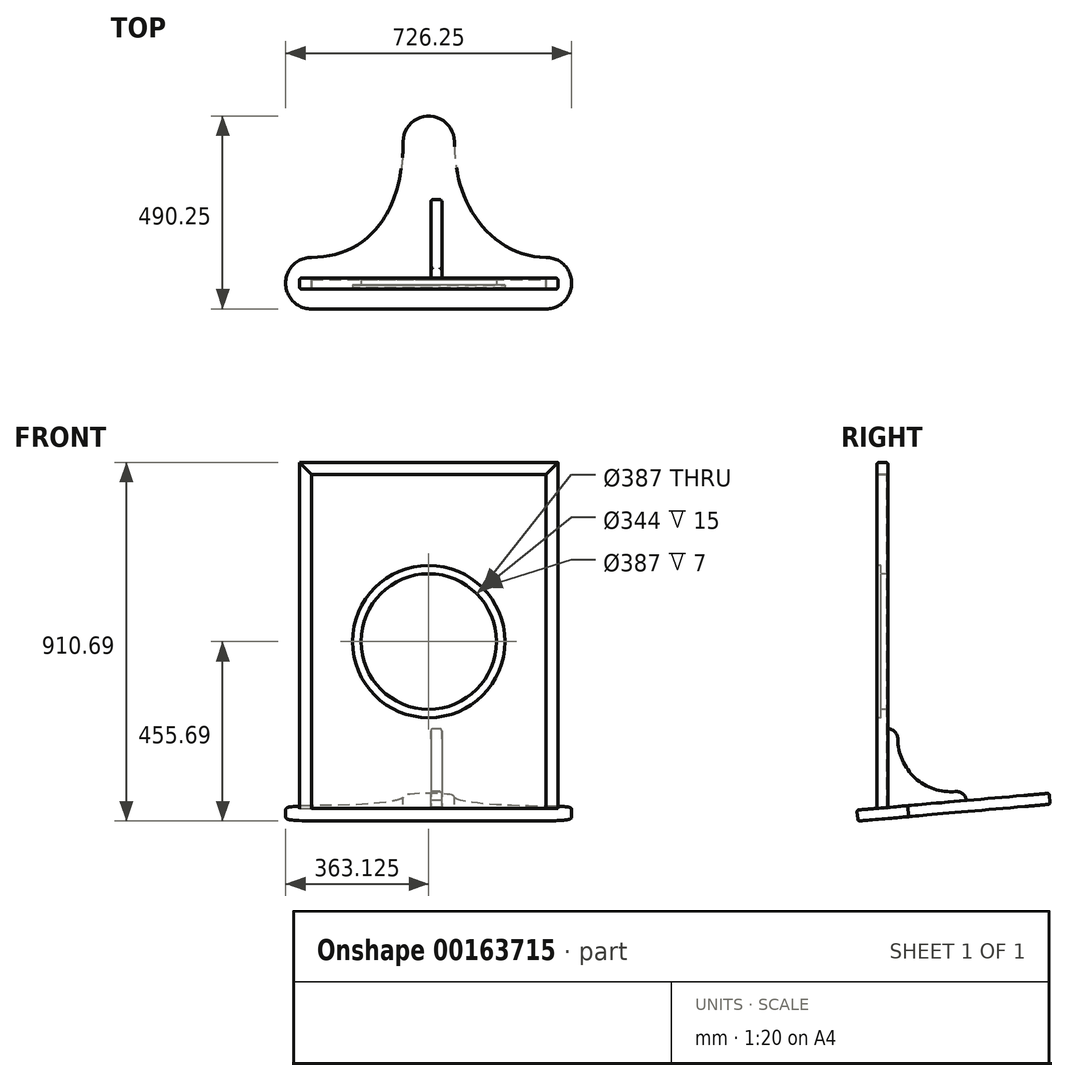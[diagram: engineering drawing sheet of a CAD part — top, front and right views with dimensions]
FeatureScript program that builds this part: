
annotation { "Feature Type Name" : "Feature", "Feature Type Description" : "" }
export const myFeature = defineFeature(function(context is Context, id is Id, definition is map)
    precondition{}
    {
        {
            var Q0;
            Q0=qCreatedBy(makeId("Front.planeOp"),FACE);
            var sketch = newSketch(context, id + "F0", { "sketchPlane" : qUnion([Q0])});
            skLineSegment(sketch, "E0.bottom", {"start": v(0, 0) * mm, "end": v(596.25, 0) * mm});
            skLineSegment(sketch, "E0.top", {"start": v(0, 850) * mm, "end": v(596.25, 850) * mm});
            skLineSegment(sketch, "E0.left", {"start": v(0, 0) * mm, "end": v(0, 850) * mm});
            skLineSegment(sketch, "E0.right", {"start": v(596.25, 0) * mm, "end": v(596.25, 850) * mm});
            skSolve(sketch);
        }
        {
            var Q0;
            Q0 = qSketchRegion(id + "F0", true);
            extrude(context, id + "F1", {"entities" : qUnion([Q0]), "depth" : (2 * 11) * mm, "symmetric" : true});
        }
        {
            var Q0;
            Q0=makeQuery(id+"F1.opExtrude","CAP_FACE",FACE,{"disambiguationData":[OSD([sQuery(id+"F0.wireOp",EDGE,"E0.bottom"),sQuery(id+"F0.wireOp",EDGE,"E0.top"),sQuery(id+"F0.wireOp",EDGE,"E0.left"),sQuery(id+"F0.wireOp",EDGE,"E0.right")])],"isStart":false});
            var sketch = newSketch(context, id + "F2", { "sketchPlane" : qUnion([Q0])});
            skLineSegment(sketch, "E1.0.0", {"start": v(596.25, 850) * mm, "end": v(0, 850) * mm});
            skLineSegment(sketch, "E1.0.1", {"start": v(0, 850) * mm, "end": v(0, 0) * mm});
            skLineSegment(sketch, "E1.0.2", {"start": v(0, 0) * mm, "end": v(596.25, 0) * mm});
            skLineSegment(sketch, "E1.0.3", {"start": v(596.25, 0) * mm, "end": v(596.25, 850) * mm});
            skSolve(sketch);
        }
        {
            var Q0;
            Q0 = qSketchRegion(id + "F2", true);
            extrude(context, id + "F3", {"entities" : qUnion([Q0]), "depth" : 3 * mm});
        }
        {
            var Q0;
            Q0=makeQuery(id+"F3.opExtrude","SWEPT_BODY",BODY,{"disambiguationData":[OSD([sQuery(id+"F2.wireOp",EDGE,"E1.0.0"),sQuery(id+"F2.wireOp",EDGE,"E1.0.1"),sQuery(id+"F2.wireOp",EDGE,"E1.0.2"),sQuery(id+"F2.wireOp",EDGE,"E1.0.3")])]});
            var Q1;
            Q1=qCreatedBy(makeId("Front.planeOp"),FACE);
            mirror(context, id + "F4", {"entities" : qUnion([Q0]), "mirrorPlane" : qUnion([Q1])});
        }
        {
            var Q0;
            Q0=qCreatedBy(makeId("Front.planeOp"),FACE);
            var sketch = newSketch(context, id + "F5", { "sketchPlane" : qUnion([Q0])});
            skLineSegment(sketch, "E2", {"start": v(-30, 0) * mm, "end": v(-30, 880) * mm});
            skLineSegment(sketch, "E3", {"start": v(-30, 880) * mm, "end": v(0, 850) * mm});
            skLineSegment(sketch, "E4", {"start": v(0, 850) * mm, "end": v(0, 0) * mm});
            skLineSegment(sketch, "E5", {"start": v(0, 0) * mm, "end": v(-30, 0) * mm});
            skLineSegment(sketch, "E6", {"start": v(596.25, 0) * mm, "end": v(596.25, 850) * mm});
            skLineSegment(sketch, "E7", {"start": v(596.25, 850) * mm, "end": v(626.25, 880) * mm});
            skLineSegment(sketch, "E8", {"start": v(626.25, 880) * mm, "end": v(626.25, 0) * mm});
            skLineSegment(sketch, "E9", {"start": v(626.25, 0) * mm, "end": v(596.25, 0) * mm});
            skSolve(sketch);
        }
        {
            var Q0;
            Q0 = qSketchRegion(id + "F5", true);
            var Q1;
            Q1=makeQuery(id+"F4.opPattern","COPY",FACE,{"derivedFrom":makeQuery(id+"F3.opExtrude","CAP_FACE",FACE,{"disambiguationData":[OSD([sQuery(id+"F2.wireOp",EDGE,"E1.0.0"),sQuery(id+"F2.wireOp",EDGE,"E1.0.1"),sQuery(id+"F2.wireOp",EDGE,"E1.0.2"),sQuery(id+"F2.wireOp",EDGE,"E1.0.3")])],"isStart":false}),"instanceName":"1"});
            extrude(context, id + "F6", {"entities" : qUnion([Q0]), "oppositeDirection" : true, "endBoundEntityFace" : qUnion([Q1]), "depth" : (2 * 11 + 2 * 3) * mm, "symmetric" : true});
        }
        {
            var Q0;
            Q0=makeQuery(id+"F3.opExtrude","CAP_FACE",FACE,{"disambiguationData":[OSD([sQuery(id+"F2.wireOp",EDGE,"E1.0.0"),sQuery(id+"F2.wireOp",EDGE,"E1.0.1"),sQuery(id+"F2.wireOp",EDGE,"E1.0.2"),sQuery(id+"F2.wireOp",EDGE,"E1.0.3")])],"isStart":false});
            var sketch = newSketch(context, id + "F7", { "sketchPlane" : qUnion([Q0])});
            skLineSegment(sketch, "E10", {"start": v(-30, 880) * mm, "end": v(0, 850) * mm});
            skLineSegment(sketch, "E11", {"start": v(0, 850) * mm, "end": v(596.25, 850) * mm});
            skLineSegment(sketch, "E12", {"start": v(596.25, 850) * mm, "end": v(626.25, 880) * mm});
            skLineSegment(sketch, "E13", {"start": v(626.25, 880) * mm, "end": v(-30, 880) * mm});
            skSolve(sketch);
        }
        {
            var Q0;
            Q0 = qSketchRegion(id + "F7", true);
            var Q1;
            Q1=makeQuery(id+"F4.opPattern","COPY",FACE,{"derivedFrom":makeQuery(id+"F3.opExtrude","CAP_FACE",FACE,{"disambiguationData":[OSD([sQuery(id+"F2.wireOp",EDGE,"E1.0.0"),sQuery(id+"F2.wireOp",EDGE,"E1.0.1"),sQuery(id+"F2.wireOp",EDGE,"E1.0.2"),sQuery(id+"F2.wireOp",EDGE,"E1.0.3")])],"isStart":false}),"instanceName":"1"});
            extrude(context, id + "F8", {"entities" : qUnion([Q0]), "endBound" : BoundingType.UP_TO_SURFACE, "oppositeDirection" : true, "endBoundEntityFace" : qUnion([Q1]), "depth" : 25 * mm});
        }
        {
            var Q0;
            Q0=makeQuery(id+"F3.opExtrude","CAP_FACE",FACE,{"disambiguationData":[OSD([sQuery(id+"F2.wireOp",EDGE,"E1.0.0"),sQuery(id+"F2.wireOp",EDGE,"E1.0.1"),sQuery(id+"F2.wireOp",EDGE,"E1.0.2"),sQuery(id+"F2.wireOp",EDGE,"E1.0.3")])],"isStart":false});
            var sketch = newSketch(context, id + "F9", { "sketchPlane" : qUnion([Q0])});
            skCircle(sketch, "E14", {"center": v(298.12, 425) * mm, "radius": 172 * mm});
            skPoint(sketch, "E14.centerSnap0", {"position": v(596.25, 425) * mm});
            skPoint(sketch, "E14.centerSnap1", {"position": v(298.12, 850) * mm});
            skSolve(sketch);
        }
        {
            var Q0;
            Q0 = qSketchRegion(id + "F9", true);
            extrude(context, id + "F10", {"entities" : qUnion([Q0]), "operationType" : NewBodyOperationType.REMOVE, "endBound" : BoundingType.THROUGH_ALL, "oppositeDirection" : true, "depth" : 25 * mm});
        }
        {
            var Q0;
            Q0=makeQuery(id+"F3.opExtrude","CAP_FACE",FACE,{"disambiguationData":[OSD([sQuery(id+"F2.wireOp",EDGE,"E1.0.0"),sQuery(id+"F2.wireOp",EDGE,"E1.0.1"),sQuery(id+"F2.wireOp",EDGE,"E1.0.2"),sQuery(id+"F2.wireOp",EDGE,"E1.0.3")])],"isStart":false});
            var sketch = newSketch(context, id + "F11", { "sketchPlane" : qUnion([Q0])});
            skCircle(sketch, "E15", {"center": v(298.12, 425) * mm, "radius": 193.5 * mm});
            skSolve(sketch);
        }
        {
            var Q0;
            Q0 = qSketchRegion(id + "F11", true);
            extrude(context, id + "F12", {"entities" : qUnion([Q0]), "operationType" : NewBodyOperationType.REMOVE, "oppositeDirection" : true, "depth" : 10 * mm});
        }
        {
            var Q0;
            Q0=makeQuery(id+"F1.opExtrude","SWEPT_FACE",FACE,{"disambiguationData":[OSD([sQuery(id+"F0.wireOp",EDGE,"E0.left")])]});
            var sketch = newSketch(context, id + "F13", { "sketchPlane" : qUnion([Q0])});
            skLineSegment(sketch, "E16", {"start": v(52.79, -2.17) * mm, "end": v(-51.83, 6.98) * mm});
            skLineSegment(sketch, "E17", {"start": v(-51.83, 6.98) * mm, "end": v(-51.83, -8.68) * mm});
            skLineSegment(sketch, "E18", {"start": v(-51.83, -8.68) * mm, "end": v(52.79, -20.76) * mm});
            skLineSegment(sketch, "E19", {"start": v(52.79, -20.76) * mm, "end": v(52.79, -2.17) * mm});
            skLineSegment(sketch, "E20", {"start": v(0, 0) * mm, "end": v(-74.05, 0) * mm, "construction": true});
            skSolve(sketch);
        }
        {
            var Q0;
            Q0 = qSketchRegion(id + "F13", true);
            extrude(context, id + "F14", {"entities" : qUnion([Q0]), "operationType" : NewBodyOperationType.REMOVE, "endBound" : BoundingType.THROUGH_ALL, "oppositeDirection" : true, "depth" : 25 * mm});
        }
        {
            var Q0;
            Q0=makeQuery(id+"F14.boolean.opBoolean","COPY",FACE,{"derivedFrom":makeQuery(id+"F14.opExtrude","SWEPT_FACE",FACE,{"disambiguationData":[OSD([sQuery(id+"F13.wireOp",EDGE,"E16")])]})});
            var sketch = newSketch(context, id + "F15", { "sketchPlane" : qUnion([Q0])});
            skLineSegment(sketch, "E21", {"start": v(0, 64.79) * mm, "end": v(596.25, 64.79) * mm});
            skLineSegment(sketch, "E22", {"start": v(596.25, -247.71) * mm, "end": v(596.25, 344.4) * mm, "construction": true});
            skLineSegment(sketch, "E23", {"start": v(298.13, 283.82) * mm, "end": v(298.13, -740.69) * mm, "construction": true});
            skLineSegment(sketch, "E24", {"start": v(0, 0) * mm, "end": v(0, -312.02) * mm, "construction": true});
            skLineSegment(sketch, "E25.0", {"start": v(0, -11.26) * mm, "end": v(0, -11.26) * mm});
            skLineSegment(sketch, "E26", {"start": v(0, 0) * mm, "end": v(0, 138.52) * mm, "construction": true});
            skArc(sketch, "E27", {"start": v(0, 64.79) * mm, "mid": v(-65, -0.21) * mm, "end": v(0, -65.21) * mm});
            skArc(sketch, "E28", {"start": v(596.25, 64.79) * mm, "mid": v(661.25, -0.21) * mm, "end": v(596.25, -65.21) * mm});
            skArc(sketch, "E29", {"start": v(233.13, -360.72) * mm, "mid": v(298.13, -425.72) * mm, "end": v(363.13, -360.72) * mm});
            skFitSpline(sketch, "E30", {"points": [v(0, -65.21) * mm, v(233.13, -360.72) * mm], "startDerivative": vector(399.52, 0) * mm, "endDerivative": vector(0, -583.63) * mm});
            skFitSpline(sketch, "E31", {"points": [v(363.13, -360.72) * mm, v(596.25, -65.21) * mm], "startDerivative": vector(0, 583.63) * mm, "endDerivative": vector(331.66, 0) * mm});
            skSolve(sketch);
        }
        {
            var Q0;
            Q0 = qSketchRegion(id + "F15", true);
            extrude(context, id + "F16", {"entities" : qUnion([Q0]), "depth" : 28 * mm});
        }
        {
            var Q0;
            Q0=qCreatedBy(makeId("Right.planeOp"),FACE);
            cPlane(context, id + "F17", {"entities" : qUnion([Q0]), "cplaneType" : CPlaneType.OFFSET, "offset" : (635 / 2) * mm, "width" : 150 * mm, "height" : 150 * mm});
        }
        {
            var Q0;
            Q0=qCreatedBy(id+"F17.planeOp",FACE);
            var sketch = newSketch(context, id + "F18", { "sketchPlane" : qUnion([Q0])});
            skLineSegment(sketch, "E32", {"start": v(14, 203.01) * mm, "end": v(14, 3.01) * mm});
            skLineSegment(sketch, "E33", {"start": v(14, 3.01) * mm, "end": v(213.16, 21.35) * mm});
            skArc(sketch, "E34", {"start": v(213.16, 21.35) * mm, "mid": v(204.27, 38.26) * mm, "end": v(186.03, 43.96) * mm});
            skArc(sketch, "E35", {"start": v(39, 178.08) * mm, "mid": v(31.65, 195.71) * mm, "end": v(14, 203.01) * mm});
            skArc(sketch, "E36", {"start": v(39, 178.08) * mm, "mid": v(83.02, 78.68) * mm, "end": v(186.03, 43.96) * mm});
            skLineSegment(sketch, "E37", {"start": v(14, 203.01) * mm, "end": v(146.15, 203.01) * mm, "construction": true});
            skLineSegment(sketch, "E38", {"start": v(213.16, 21.35) * mm, "end": v(201.52, 147.7) * mm, "construction": true});
            skSolve(sketch);
        }
        {
            var Q0;
            Q0 = qSketchRegion(id + "F18", true);
            extrude(context, id + "F19", {"entities" : qUnion([Q0]), "depth" : 28 * mm, "symmetric" : true});
        }
        {
            var Q0;
            Q0=makeQuery(id+"F6.opExtrude","CAP_EDGE",EDGE,{"disambiguationData":[OSD([sQuery(id+"F5.wireOp",EDGE,"E8")])],"isStart":true});
            var Q1;
            Q1=makeQuery(id+"F8.opExtrude","CAP_EDGE",EDGE,{"disambiguationData":[OSD([sQuery(id+"F7.wireOp",EDGE,"E13")])],"isStart":true});
            var Q2;
            Q2=makeQuery(id+"F6.opExtrude","CAP_EDGE",EDGE,{"disambiguationData":[OSD([sQuery(id+"F5.wireOp",EDGE,"E2")])],"isStart":true});
            var Q3;
            Q3=makeQuery(id+"F6.opExtrude","CAP_EDGE",EDGE,{"disambiguationData":[OSD([sQuery(id+"F5.wireOp",EDGE,"E2")])],"isStart":false});
            var Q4;
            Q4=makeQuery(id+"F8.opExtrude","CAP_EDGE",EDGE,{"disambiguationData":[OSD([sQuery(id+"F7.wireOp",EDGE,"E13")])],"isStart":false});
            var Q5;
            Q5=makeQuery(id+"F6.opExtrude","CAP_EDGE",EDGE,{"disambiguationData":[OSD([sQuery(id+"F5.wireOp",EDGE,"E8")])],"isStart":false});
            fillet(context, id + "F20", {"entities" : qUnion([Q0, Q1, Q2, Q3, Q4, Q5]), "radius" : 5 * mm, "tangentPropagation" : true, "allowEdgeOverflow" : false});
        }
        {
            var Q0;
            Q0=makeQuery(id+"F16.opExtrude","CAP_FACE",FACE,{"disambiguationData":[OSD([sQuery(id+"F15.wireOp",EDGE,"E21"),sQuery(id+"F15.wireOp",EDGE,"E27"),sQuery(id+"F15.wireOp",EDGE,"E28"),sQuery(id+"F15.wireOp",EDGE,"E29"),sQuery(id+"F15.wireOp",EDGE,"E30"),sQuery(id+"F15.wireOp",EDGE,"E31")])],"isStart":true});
            var Q1;
            Q1=makeQuery(id+"F16.opExtrude","CAP_FACE",FACE,{"disambiguationData":[OSD([sQuery(id+"F15.wireOp",EDGE,"E21"),sQuery(id+"F15.wireOp",EDGE,"E27"),sQuery(id+"F15.wireOp",EDGE,"E28"),sQuery(id+"F15.wireOp",EDGE,"E29"),sQuery(id+"F15.wireOp",EDGE,"E30"),sQuery(id+"F15.wireOp",EDGE,"E31")])],"isStart":false});
            fillet(context, id + "F21", {"entities" : qUnion([Q0, Q1]), "radius" : 5 * mm, "tangentPropagation" : true, "allowEdgeOverflow" : false});
        }
        {
            var Q0;
            Q0=makeQuery(id+"F19.opExtrude","CAP_EDGE",EDGE,{"disambiguationData":[OSD([sQuery(id+"F18.wireOp",EDGE,"E36")])],"isStart":true});
            var Q1;
            Q1=makeQuery(id+"F19.opExtrude","CAP_EDGE",EDGE,{"disambiguationData":[OSD([sQuery(id+"F18.wireOp",EDGE,"E36")])],"isStart":false});
            fillet(context, id + "F22", {"entities" : qUnion([Q0, Q1]), "radius" : 5 * mm, "tangentPropagation" : true, "allowEdgeOverflow" : false});
        }
        {
            var Q0;
            Q0=makeQuery(id+"F10.boolean.opBoolean","INTERSECT",EDGE,{"derivedFrom":[makeQuery(id+"F4.opPattern","COPY",FACE,{"derivedFrom":makeQuery(id+"F3.opExtrude","CAP_FACE",FACE,{"disambiguationData":[OSD([sQuery(id+"F2.wireOp",EDGE,"E1.0.0"),sQuery(id+"F2.wireOp",EDGE,"E1.0.1"),sQuery(id+"F2.wireOp",EDGE,"E1.0.2"),sQuery(id+"F2.wireOp",EDGE,"E1.0.3")])],"isStart":false}),"instanceName":"1"}),makeQuery(id+"F10.opExtrude","SWEPT_FACE",FACE,{"disambiguationData":[OSD([sQuery(id+"F9.wireOp",EDGE,"E14")])]})]});
            fillet(context, id + "F23", {"entities" : qUnion([Q0]), "radius" : 5 * mm, "tangentPropagation" : true, "allowEdgeOverflow" : false});
        }
    });
